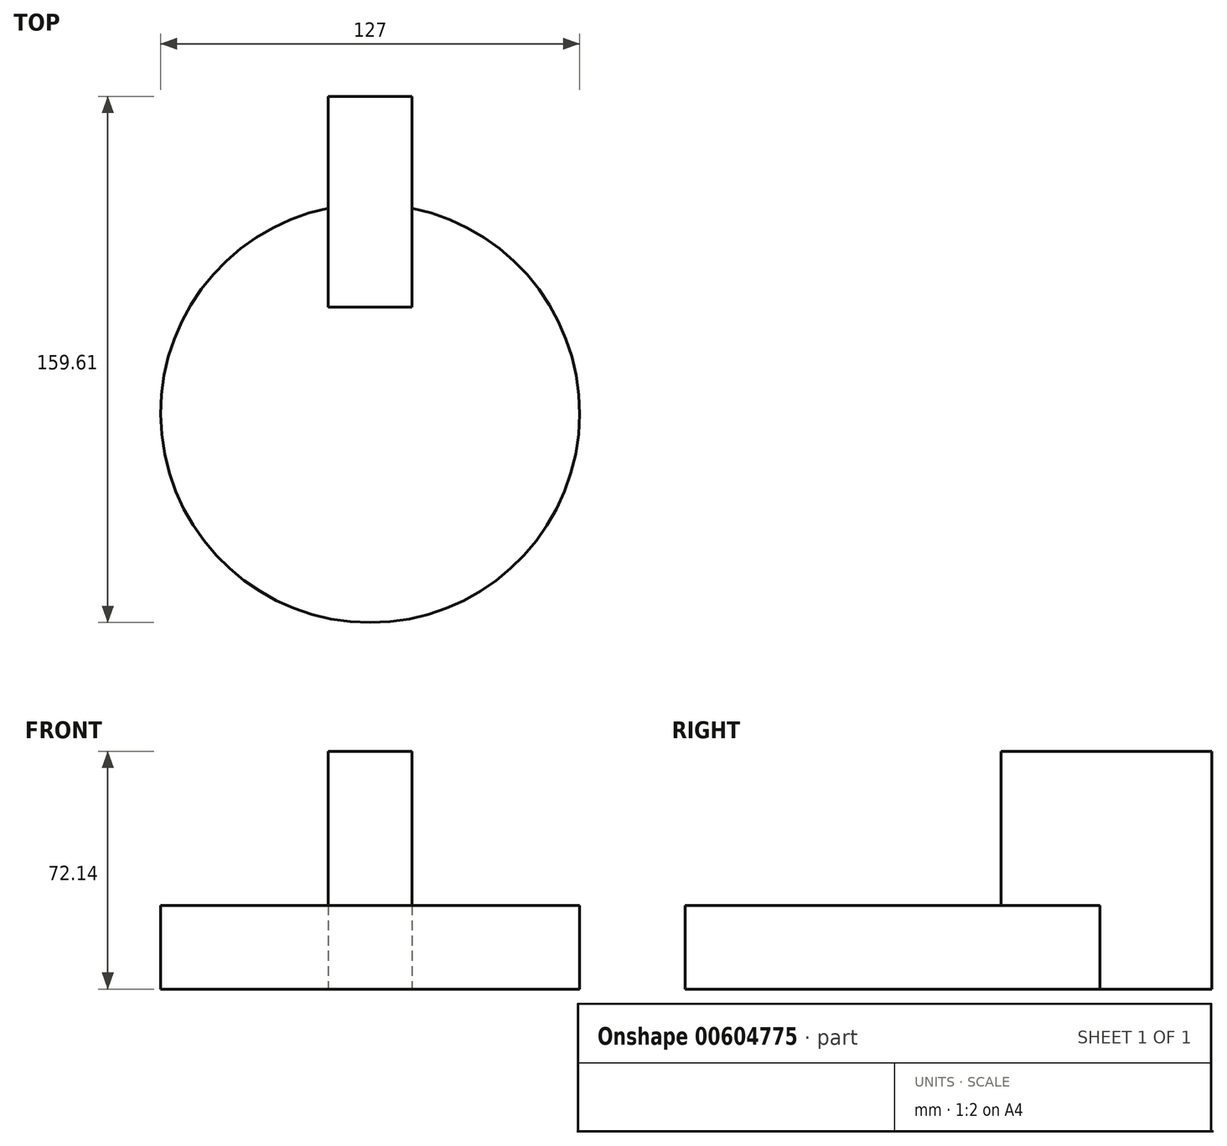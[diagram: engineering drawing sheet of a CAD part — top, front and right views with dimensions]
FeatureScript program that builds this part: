
annotation { "Feature Type Name" : "Feature", "Feature Type Description" : "" }
export const myFeature = defineFeature(function(context is Context, id is Id, definition is map)
    precondition{}
    {
        {
            var Q0;
            Q0=qCreatedBy(makeId("Top.planeOp"),FACE);
            var sketch = newSketch(context, id + "F0", { "sketchPlane" : qUnion([Q0])});
            skCircle(sketch, "E0", {"center": v(0, 0) * mm, "radius": 63.5 * mm});
            skSolve(sketch);
        }
        {
            var Q0;
            Q0=makeQuery(id+"F0.imprint","IMPRINT",FACE,{"disambiguationData":[TD([[makeQuery(id+"F0.imprint","IMPRINT",EDGE,{"derivedFrom":sQuery(id+"F0.wireOp",EDGE,"E0")}),1.0]])]});
            extrude(context, id + "F1", {"entities" : qUnion([Q0]), "depth" : 25.4 * mm, "offsetDistance" : 25.4 * mm});
        }
        {
            var Q0;
            Q0=qCreatedBy(makeId("Right.planeOp"),FACE);
            var sketch = newSketch(context, id + "F2", { "sketchPlane" : qUnion([Q0])});
            skLineSegment(sketch, "E1", {"start": v(32.2, 0) * mm, "end": v(32.2, 72.14) * mm});
            skLineSegment(sketch, "E2", {"start": v(32.2, 72.14) * mm, "end": v(96.11, 72.14) * mm});
            skLineSegment(sketch, "E3", {"start": v(96.11, 72.14) * mm, "end": v(96.11, 0) * mm});
            skLineSegment(sketch, "E4", {"start": v(96.11, 0) * mm, "end": v(32.2, 0) * mm});
            skSolve(sketch);
        }
        {
            var Q0;
            Q0=makeQuery(id+"F2.imprint","IMPRINT",FACE,{"disambiguationData":[TD([[makeQuery(id+"F2.imprint","IMPRINT",EDGE,{"derivedFrom":sQuery(id+"F2.wireOp",EDGE,"E1")}),-1.0]])]});
            extrude(context, id + "F3", {"entities" : qUnion([Q0]), "operationType" : NewBodyOperationType.ADD, "endBound" : BoundingType.SYMMETRIC, "depth" : 25.4 * mm, "offsetDistance" : 25.4 * mm});
        }
    });
